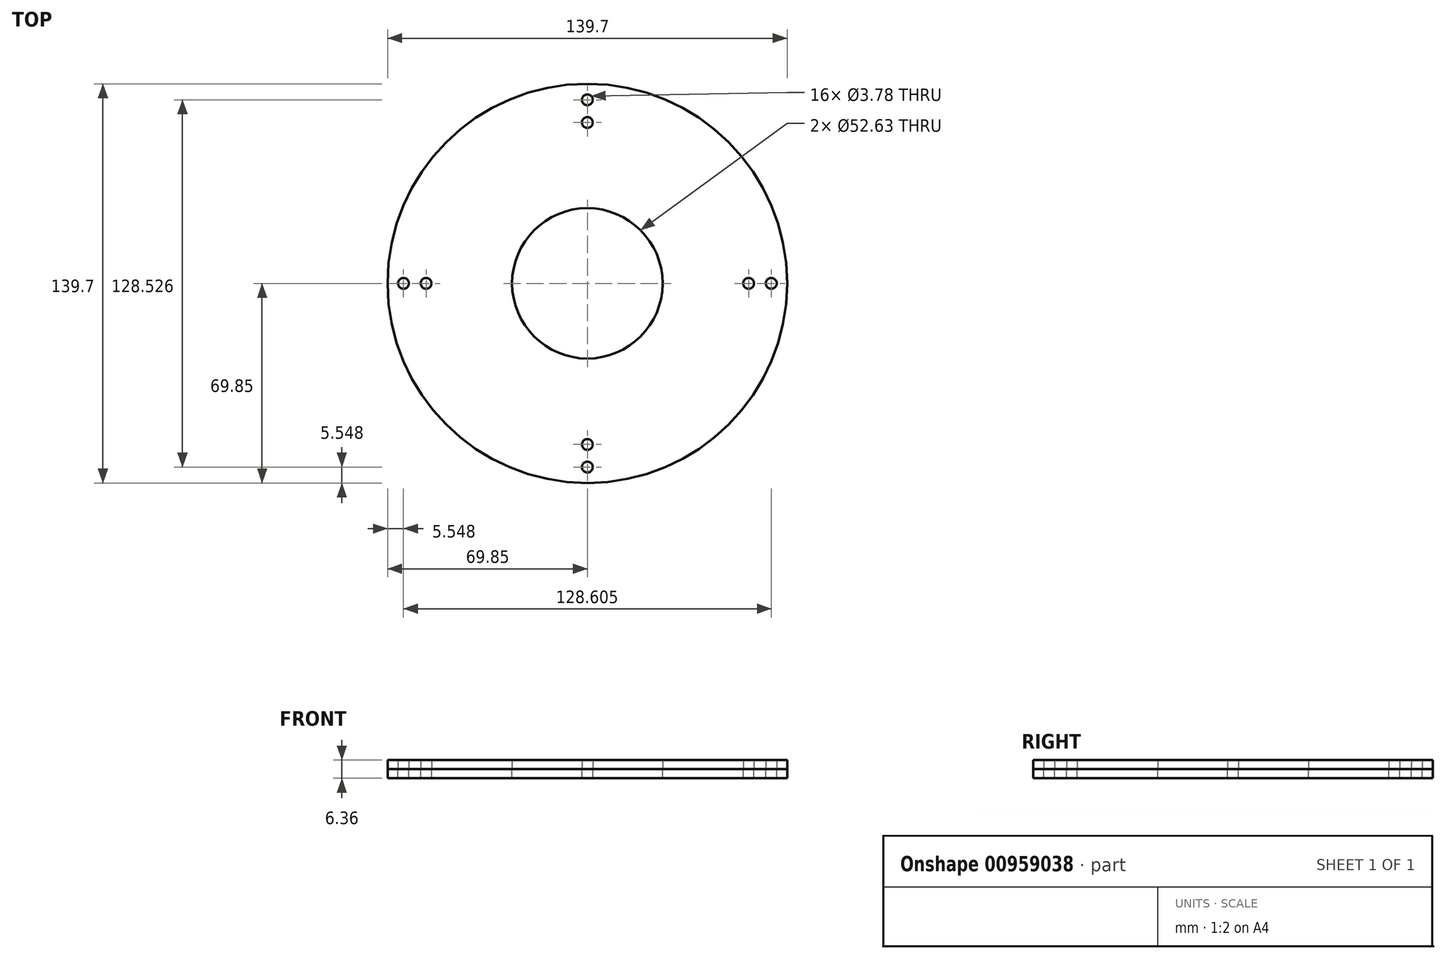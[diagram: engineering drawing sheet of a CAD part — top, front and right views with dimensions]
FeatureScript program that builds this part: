
annotation { "Feature Type Name" : "Feature", "Feature Type Description" : "" }
export const myFeature = defineFeature(function(context is Context, id is Id, definition is map)
    precondition{}
    {
        {
            var Q0;
            Q0=qCreatedBy(makeId("Top.planeOp"),FACE);
            var sketch = newSketch(context, id + "F0", { "sketchPlane" : qUnion([Q0])});
            skCircle(sketch, "E0", {"center": v(0, 0) * mm, "radius": 69.85 * mm});
            skCircle(sketch, "E1", {"center": v(0, 0) * mm, "radius": 26.31 * mm});
            skCircle(sketch, "E2", {"center": v(0, 64.22) * mm, "radius": 1.9 * mm});
            skCircle(sketch, "E3", {"center": v(0, 56.3) * mm, "radius": 1.9 * mm});
            skCircle(sketch, "E4", {"center": v(64.3, 0) * mm, "radius": 1.9 * mm});
            skCircle(sketch, "E5", {"center": v(56.38, 0) * mm, "radius": 1.9 * mm});
            skCircle(sketch, "E6", {"center": v(-64.3, 0) * mm, "radius": 1.9 * mm});
            skCircle(sketch, "E7", {"center": v(-56.38, 0) * mm, "radius": 1.9 * mm});
            skCircle(sketch, "E8", {"center": v(0, -64.3) * mm, "radius": 1.9 * mm});
            skCircle(sketch, "E9", {"center": v(0, -56.38) * mm, "radius": 1.9 * mm});
            skSolve(sketch);
        }
        {
            var Q0;
            Q0 = qSketchRegion(id + "F0", true);
            var Q1;
            Q1 = qSketchRegion(id + "F2", true);
            var Q2;
            Q2 = qSketchRegion(id + "F4", true);
            extrude(context, id + "F1", {"entities" : qUnion([Q0, Q1, Q2]), "oppositeDirection" : true, "depth" : 3.17 * mm, "offsetDistance" : 25.4 * mm});
        }
        {
            var Q0;
            Q0=qCreatedBy(makeId("Top.planeOp"),FACE);
            var sketch = newSketch(context, id + "F2", { "sketchPlane" : qUnion([Q0])});
            skCircle(sketch, "E10", {"center": v(0, 46.84) * mm, "radius": 1.35 * mm});
            skCircle(sketch, "E11", {"center": v(-40.56, -23.42) * mm, "radius": 1.35 * mm});
            skCircle(sketch, "E12", {"center": v(40.56, -23.42) * mm, "radius": 1.35 * mm});
            skSolve(sketch);
        }
        {
            var Q0;
            Q0 = qSketchRegion(id + "F0", true);
            extrude(context, id + "F3", {"entities" : qUnion([Q0]), "depth" : 3.17 * mm, "offsetDistance" : 25.4 * mm});
        }
    });
